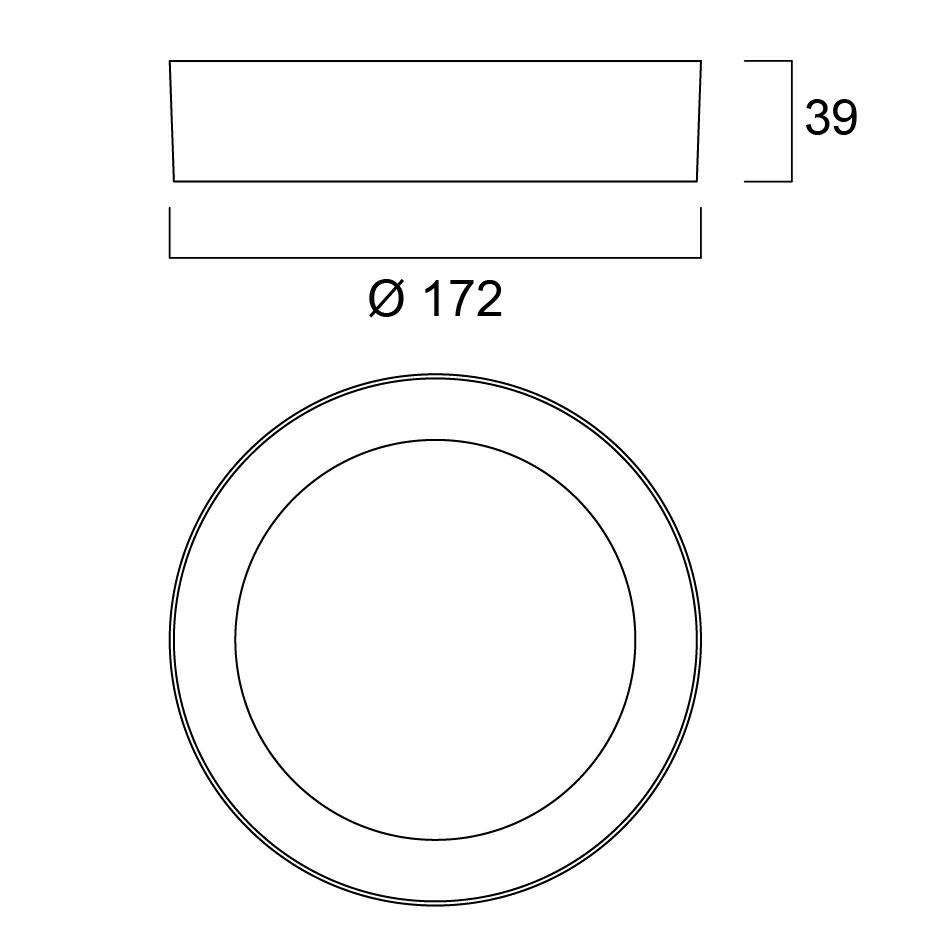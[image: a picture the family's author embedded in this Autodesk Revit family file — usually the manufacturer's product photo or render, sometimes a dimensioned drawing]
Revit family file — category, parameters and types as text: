
# Revit family: 0053899
name_source: partatom
category: Lighting Fixtures
revit_build: Autodesk Revit 2016 (Build: 20150220_1215(x64)
units: mm (PartAtom-declared; Revit-internal decimal feet)

## family parameters
Cut with Voids When Loaded = No
Host = Face
Light Source = Yes
OmniClass Number = 23.80.70.00
OmniClass Title = Lighting
Part Type = Normal
Room Calculation Point = No
Round Connector Dimension = Use Diameter
Shared = No

## types (1)
- 0053899 ST eco Downlight Flat 172 1050lm 830 DIM S
    Apparent Load = 13 VA
    Assembly Code = D5020200
    AssetType = Fixed
    ClassificationName = Uniclass2015
    ClassificationValue = EF_70_80
    Color Filter = 16777215
    Cost = 0 $
    Default Elevation = 1219 mm
    Description = Integrated LED surface mounted downlight providing 1040 fixture lumens at a wattage of 13W giving a high efficacy of 80lm/W. Fitting includes Leading/Trailing edge phase dimmable driver and has a round outer dimmension of of 172x172x39mm with an IP20 and IK02 rating providing uniform distribution with an Opal diffuser and 110° beam angle. Provided including a Loop in Loop out box and built with a white aluminium housing.
    Dimming Lamp Color Temperature Shift = <None>
    DimmingControlOptions = Dimmable
    DocumentationLiterature = http://www.sylvania-lighting.com
    DurationUnit = hours
    ElectricShockClassification = Class II
    Emit Shape Visible in Rendering = No
    Emit from Circle Diameter = 129 mm
    ExpectedLife = 50000
    IfcExportAs = IfcLightFixtureType
    IfcExportType = IfcLightFixtureType
    ImpactProtectionIndex = IK06
    IngressProtection = IP20
    InputNominalFrequency = 50/60 Hz
    InputVoltage = 220-240V~
    Keynote = 16500
    Lamp = LED
    LampColourRenderingIndex = 80
    LampColourTemperature = 3000 K
    LampNominalLuminous = 1050 lm
    LampsType = LED
    LuminousEfficacy = 80.76 lm/W
    Manufacturer = Feilo Sylvania
    ManufacturerName = Feilo Sylvania
    Material = aluminium housing, polystyrene diffuser
    Material_1_FEILO = Body-Sylvania-SylflatSurface-White
    Material_2_FEILO = LED-Sylvania-SylflatSurface
    Material_3_FEILO = <By Category>
    Material_4_FEILO = <By Category>
    Model = ST eco Downlight Flat 172 1050lm 830 DIM S
    ModelNumber = 0053899
    ModelReference = ST eco Downlight Flat 172 1050lm 830 DIM S
    Name = ST eco Downlight Flat 172 1050lm 830 DIM S
    NominalDepth = 172 mm  [stored 0.564304 ft]
    NominalHeight = 39 mm  [stored 0.127953 ft]
    NominalLength = 172 mm  [stored 0.564304 ft]
    Photometric Web File = 0053899.ies
    PowerConsumption = 13 W
    PowerFactor = 0.9
    RadiusDiffuser_FEILO = 7 mm  [stored 0.0229659 ft]
    RadiusSquare_FEILO = 10 mm  [stored 0.0328084 ft]
    Round_FEILO = Yes
    Square_FEILO = No
    Tilt Angle = -90.00°
    Type Image = <None>
    TypeName = ST eco Downlight Flat 172 1050lm 830 DIM S
    URL = http://www.sylvania-lighting.com
    Voltage = 230 V
    Weight = 10.26 kg
    WidthDiffuser_FEILO = 129 mm
    Width_FEILO = 172 mm  [stored 0.564304 ft]

note: [stored X ft] marks values corroborated as IEEE doubles in the binary element streams (Revit-internal decimal feet)

## geometry (parser evidence)
native form markers: Sweep x1
no freeform markers — native parametric forms only
